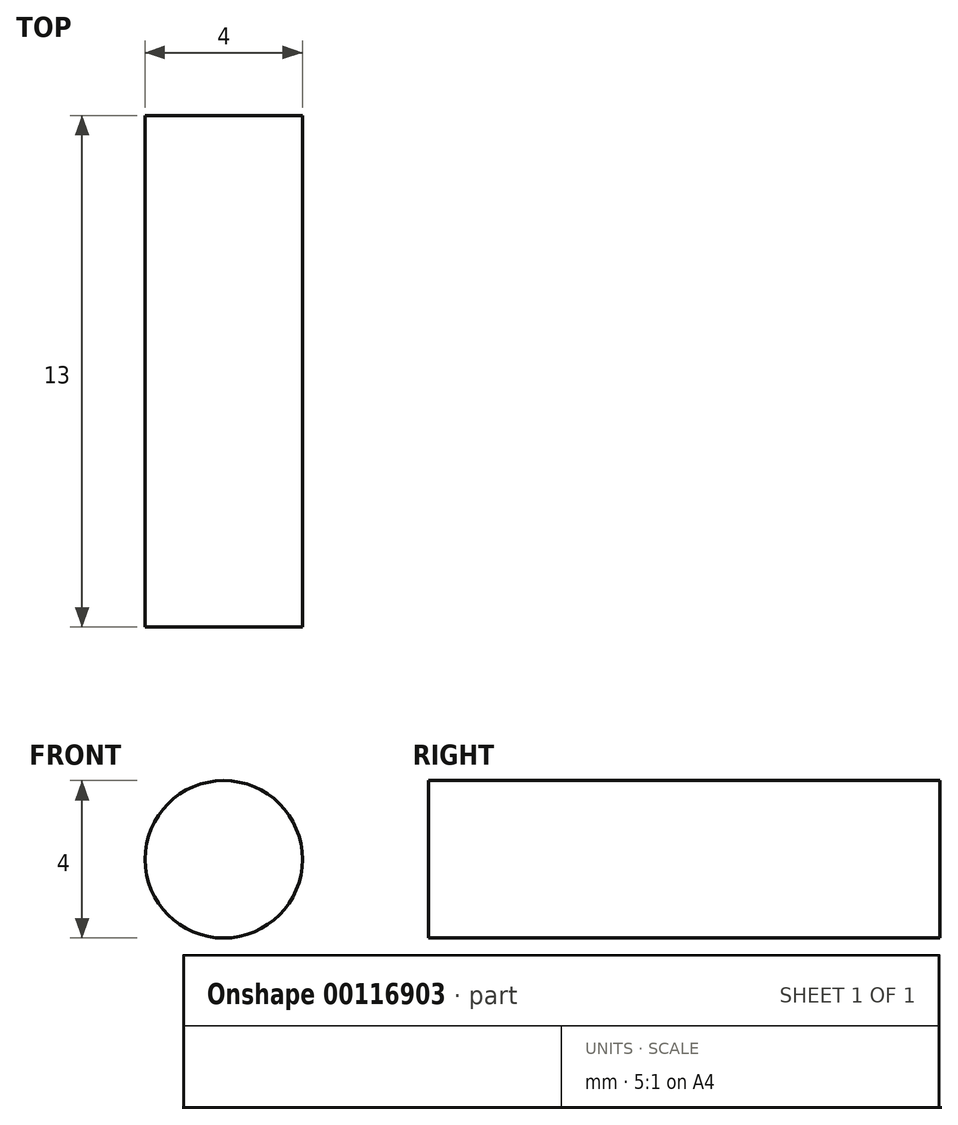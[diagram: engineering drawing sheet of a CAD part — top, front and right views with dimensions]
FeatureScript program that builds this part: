
annotation { "Feature Type Name" : "Feature", "Feature Type Description" : "" }
export const myFeature = defineFeature(function(context is Context, id is Id, definition is map)
    precondition{}
    {
        {
            var Q0;
            Q0=qCreatedBy(makeId("Front.planeOp"),FACE);
            var sketch = newSketch(context, id + "F0", { "sketchPlane" : qUnion([Q0])});
            skCircle(sketch, "E0", {"center": v(0, 0) * mm, "radius": 2 * mm});
            skSolve(sketch);
        }
        {
            var Q0;
            Q0 = qSketchRegion(id + "F0", true);
            var Q1;
            Q1=makeQuery(id+"F0.imprint","IMPRINT",FACE,{"disambiguationData":[TD([[makeQuery(id+"F0.imprint","IMPRINT",EDGE,{"derivedFrom":sQuery(id+"F0.wireOp",EDGE,"E0")}),1.0]])]});
            extrude(context, id + "F1", {"entities" : qUnion([Q0, Q1]), "depth" : 13 * mm});
        }
    });
